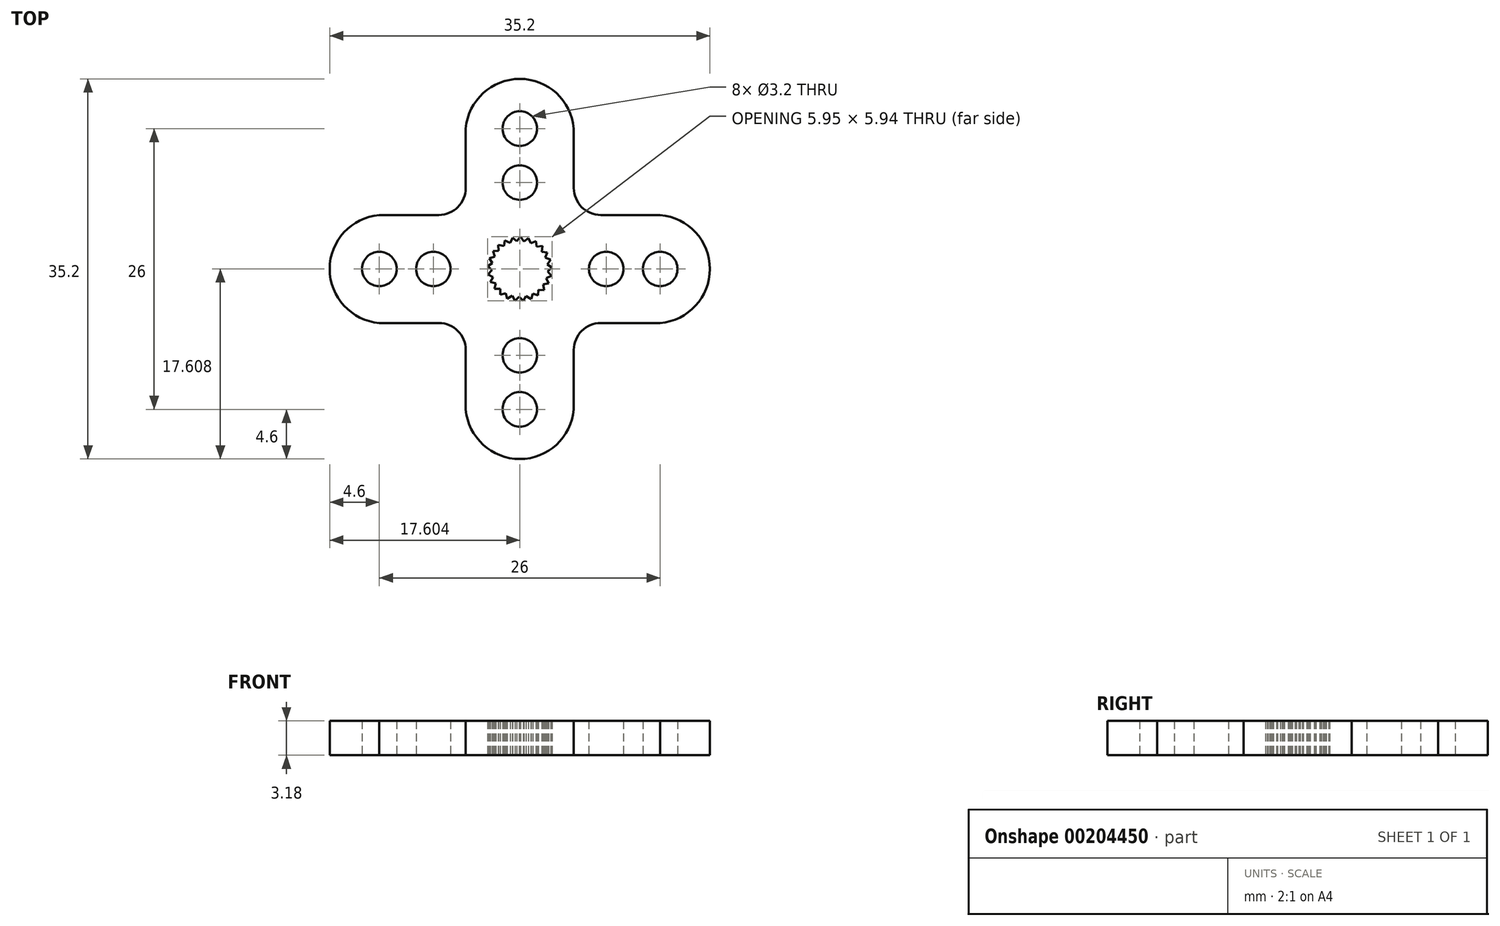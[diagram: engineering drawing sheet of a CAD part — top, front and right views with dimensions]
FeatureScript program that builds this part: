
annotation { "Feature Type Name" : "Feature", "Feature Type Description" : "" }
export const myFeature = defineFeature(function(context is Context, id is Id, definition is map)
    precondition{}
    {
        {
            var Q0;
            Q0=qCreatedBy(makeId("Top.planeOp"),FACE);
            var sketch = newSketch(context, id + "F0", { "sketchPlane" : qUnion([Q0])});
            skCircle(sketch, "E0", {"center": v(0, 13) * mm, "radius": 1.6 * mm});
            skCircle(sketch, "E1.0.1.0", {"center": v(0, 8) * mm, "radius": 1.6 * mm});
            skLineSegment(sketch, "E1.direction1", {"start": v(0, 13) * mm, "end": v(25, 13) * mm, "construction": true});
            skLineSegment(sketch, "E1.direction2", {"start": v(0, 13) * mm, "end": v(0, 8) * mm, "construction": true});
            skArc(sketch, "E2", {"start": v(5, 13) * mm, "mid": v(3.4, 16.28) * mm, "end": v(0, 17.6) * mm});
            skArc(sketch, "E3.MirrorCS", {"start": v(-5, 13) * mm, "mid": v(-3.4, 16.28) * mm, "end": v(0, 17.6) * mm});
            skPoint(sketch, "E4.center", {"position": v(0, 0) * mm});
            skLineSegment(sketch, "E5.trimOffspring", {"start": v(5, 7.5) * mm, "end": v(5, 13) * mm});
            skLineSegment(sketch, "E6.trimOffspring", {"start": v(-5, 7.5) * mm, "end": v(-5, 13) * mm});
            skArc(sketch, "E7", {"start": v(5, 7.5) * mm, "mid": v(5.73, 5.73) * mm, "end": v(7.5, 5) * mm});
            skArc(sketch, "E8.1.0", {"start": v(-7.5, 5) * mm, "mid": v(-5.73, 5.73) * mm, "end": v(-5, 7.5) * mm});
            skLineSegment(sketch, "E9", {"start": v(-2.48, 1.65) * mm, "end": v(-2.31, 1.15) * mm});
            skLineSegment(sketch, "E10", {"start": v(-2.31, 1.15) * mm, "end": v(-2.81, 0.98) * mm});
            skLineSegment(sketch, "E11.1.0", {"start": v(-2.81, 0.98) * mm, "end": v(-2.53, 0.54) * mm});
            skLineSegment(sketch, "E11.1.1", {"start": v(-2.53, 0.54) * mm, "end": v(-2.97, 0.25) * mm});
            skLineSegment(sketch, "E11.2.0", {"start": v(-2.97, 0.25) * mm, "end": v(-2.58, -0.1) * mm});
            skLineSegment(sketch, "E11.2.1", {"start": v(-2.58, -0.1) * mm, "end": v(-2.94, -0.5) * mm});
            skLineSegment(sketch, "E11.3.0", {"start": v(-2.94, -0.5) * mm, "end": v(-2.47, -0.74) * mm});
            skLineSegment(sketch, "E11.3.1", {"start": v(-2.47, -0.74) * mm, "end": v(-2.72, -1.2) * mm});
            skLineSegment(sketch, "E11.4.0", {"start": v(-2.72, -1.2) * mm, "end": v(-2.21, -1.34) * mm});
            skLineSegment(sketch, "E11.4.1", {"start": v(-2.21, -1.34) * mm, "end": v(-2.34, -1.85) * mm});
            skLineSegment(sketch, "E11.5.0", {"start": v(-2.34, -1.85) * mm, "end": v(-1.8, -1.84) * mm});
            skLineSegment(sketch, "E11.5.1", {"start": v(-1.8, -1.84) * mm, "end": v(-1.8, -2.37) * mm});
            skLineSegment(sketch, "E11.6.0", {"start": v(-1.8, -2.37) * mm, "end": v(-1.3, -2.24) * mm});
            skLineSegment(sketch, "E11.6.1", {"start": v(-1.3, -2.24) * mm, "end": v(-1.16, -2.75) * mm});
            skLineSegment(sketch, "E11.7.0", {"start": v(-1.16, -2.75) * mm, "end": v(-0.7, -2.49) * mm});
            skLineSegment(sketch, "E11.7.1", {"start": v(-0.7, -2.49) * mm, "end": v(-0.44, -2.95) * mm});
            skLineSegment(sketch, "E11.8.0", {"start": v(-0.44, -2.95) * mm, "end": v(-0.06, -2.58) * mm});
            skLineSegment(sketch, "E11.8.1", {"start": v(-0.06, -2.58) * mm, "end": v(0.3, -2.96) * mm});
            skLineSegment(sketch, "E11.9.0", {"start": v(0.3, -2.96) * mm, "end": v(0.59, -2.52) * mm});
            skLineSegment(sketch, "E11.9.1", {"start": v(0.59, -2.52) * mm, "end": v(1.04, -2.8) * mm});
            skLineSegment(sketch, "E11.10.0", {"start": v(1.04, -2.8) * mm, "end": v(1.2, -2.3) * mm});
            skLineSegment(sketch, "E11.10.1", {"start": v(1.2, -2.3) * mm, "end": v(1.7, -2.45) * mm});
            skLineSegment(sketch, "E11.11.0", {"start": v(1.7, -2.45) * mm, "end": v(1.73, -1.92) * mm});
            skLineSegment(sketch, "E11.11.1", {"start": v(1.73, -1.92) * mm, "end": v(2.25, -1.95) * mm});
            skLineSegment(sketch, "E11.12.0", {"start": v(2.25, -1.95) * mm, "end": v(2.15, -1.43) * mm});
            skLineSegment(sketch, "E11.12.1", {"start": v(2.15, -1.43) * mm, "end": v(2.67, -1.33) * mm});
            skLineSegment(sketch, "E11.13.0", {"start": v(2.67, -1.33) * mm, "end": v(2.44, -0.85) * mm});
            skLineSegment(sketch, "E11.13.1", {"start": v(2.44, -0.85) * mm, "end": v(2.91, -0.62) * mm});
            skLineSegment(sketch, "E11.14.0", {"start": v(2.91, -0.62) * mm, "end": v(2.57, -0.22) * mm});
            skLineSegment(sketch, "E11.14.1", {"start": v(2.57, -0.22) * mm, "end": v(2.98, 0.12) * mm});
            skLineSegment(sketch, "E11.15.0", {"start": v(2.98, 0.12) * mm, "end": v(2.55, 0.43) * mm});
            skLineSegment(sketch, "E11.15.1", {"start": v(2.55, 0.43) * mm, "end": v(2.85, 0.86) * mm});
            skLineSegment(sketch, "E11.16.0", {"start": v(2.85, 0.86) * mm, "end": v(2.36, 1.05) * mm});
            skLineSegment(sketch, "E11.16.1", {"start": v(2.36, 1.05) * mm, "end": v(2.55, 1.54) * mm});
            skLineSegment(sketch, "E11.17.0", {"start": v(2.55, 1.54) * mm, "end": v(2.03, 1.6) * mm});
            skLineSegment(sketch, "E11.17.1", {"start": v(2.03, 1.6) * mm, "end": v(2.09, 2.13) * mm});
            skLineSegment(sketch, "E11.18.0", {"start": v(2.09, 2.13) * mm, "end": v(1.56, 2.06) * mm});
            skLineSegment(sketch, "E11.18.1", {"start": v(1.56, 2.06) * mm, "end": v(1.5, 2.58) * mm});
            skLineSegment(sketch, "E11.19.0", {"start": v(1.5, 2.58) * mm, "end": v(1, 2.38) * mm});
            skLineSegment(sketch, "E11.19.1", {"start": v(1, 2.38) * mm, "end": v(0.8, 2.87) * mm});
            skLineSegment(sketch, "E11.20.0", {"start": v(0.8, 2.87) * mm, "end": v(0.38, 2.56) * mm});
            skLineSegment(sketch, "E11.20.1", {"start": v(0.38, 2.56) * mm, "end": v(0.07, 2.98) * mm});
            skLineSegment(sketch, "E11.21.0", {"start": v(0.07, 2.98) * mm, "end": v(-0.27, 2.57) * mm});
            skLineSegment(sketch, "E11.21.1", {"start": v(-0.27, 2.57) * mm, "end": v(-0.68, 2.9) * mm});
            skLineSegment(sketch, "E11.22.0", {"start": v(-0.68, 2.9) * mm, "end": v(-0.9, 2.42) * mm});
            skLineSegment(sketch, "E11.22.1", {"start": v(-0.9, 2.42) * mm, "end": v(-1.38, 2.64) * mm});
            skLineSegment(sketch, "E11.23.0", {"start": v(-1.38, 2.64) * mm, "end": v(-1.47, 2.12) * mm});
            skLineSegment(sketch, "E11.23.1", {"start": v(-1.47, 2.12) * mm, "end": v(-2, 2.22) * mm});
            skLineSegment(sketch, "E11.24.0", {"start": v(-2, 2.22) * mm, "end": v(-1.95, 1.69) * mm});
            skLineSegment(sketch, "E11.24.1", {"start": v(-1.95, 1.69) * mm, "end": v(-2.48, 1.65) * mm});
            skCircle(sketch, "E12.1.0", {"center": v(-13, 0) * mm, "radius": 1.6 * mm});
            skCircle(sketch, "E12.1.1", {"center": v(-8, 0) * mm, "radius": 1.6 * mm});
            skLineSegment(sketch, "E12.1.2", {"start": v(-13, 0) * mm, "end": v(-8, 0) * mm, "construction": true});
            skLineSegment(sketch, "E12.1.5", {"start": v(-7.5, 5) * mm, "end": v(-13, 5) * mm});
            skArc(sketch, "E12.1.6", {"start": v(-5, -7.5) * mm, "mid": v(-5.73, -5.73) * mm, "end": v(-7.5, -5) * mm});
            skLineSegment(sketch, "E12.1.9", {"start": v(-7.5, -5) * mm, "end": v(-13, -5) * mm});
            skArc(sketch, "E12.1.10", {"start": v(-13, -5) * mm, "mid": v(-16.28, -3.4) * mm, "end": v(-17.6, 0) * mm});
            skArc(sketch, "E12.1.11", {"start": v(-13, 5) * mm, "mid": v(-16.28, 3.4) * mm, "end": v(-17.6, 0) * mm});
            skCircle(sketch, "E12.2.0", {"center": v(0, -13) * mm, "radius": 1.6 * mm});
            skCircle(sketch, "E12.2.1", {"center": v(0, -8) * mm, "radius": 1.6 * mm});
            skLineSegment(sketch, "E12.2.2", {"start": v(0, -13) * mm, "end": v(0, -8) * mm, "construction": true});
            skArc(sketch, "E12.2.3", {"start": v(-5, -7.5) * mm, "mid": v(-5.73, -5.73) * mm, "end": v(-7.5, -5) * mm});
            skLineSegment(sketch, "E12.2.5", {"start": v(-5, -7.5) * mm, "end": v(-5, -13) * mm});
            skArc(sketch, "E12.2.6", {"start": v(7.5, -5) * mm, "mid": v(5.73, -5.73) * mm, "end": v(5, -7.5) * mm});
            skLineSegment(sketch, "E12.2.9", {"start": v(5, -7.5) * mm, "end": v(5, -13) * mm});
            skArc(sketch, "E12.2.10", {"start": v(5, -13) * mm, "mid": v(3.4, -16.28) * mm, "end": v(0, -17.6) * mm});
            skArc(sketch, "E12.2.11", {"start": v(-5, -13) * mm, "mid": v(-3.4, -16.28) * mm, "end": v(0, -17.6) * mm});
            skCircle(sketch, "E12.3.0", {"center": v(13, 0) * mm, "radius": 1.6 * mm});
            skCircle(sketch, "E12.3.1", {"center": v(8, 0) * mm, "radius": 1.6 * mm});
            skLineSegment(sketch, "E12.3.2", {"start": v(13, 0) * mm, "end": v(8, 0) * mm, "construction": true});
            skArc(sketch, "E12.3.3", {"start": v(7.5, -5) * mm, "mid": v(5.73, -5.73) * mm, "end": v(5, -7.5) * mm});
            skLineSegment(sketch, "E12.3.5", {"start": v(7.5, -5) * mm, "end": v(13, -5) * mm});
            skLineSegment(sketch, "E12.3.9", {"start": v(7.5, 5) * mm, "end": v(13, 5) * mm});
            skArc(sketch, "E12.3.10", {"start": v(13, 5) * mm, "mid": v(16.28, 3.4) * mm, "end": v(17.6, 0) * mm});
            skArc(sketch, "E12.3.11", {"start": v(13, -5) * mm, "mid": v(16.28, -3.4) * mm, "end": v(17.6, 0) * mm});
            skSolve(sketch);
        }
        {
            var Q0;
            Q0 = qSketchRegion(id + "F0", true);
            extrude(context, id + "F1", {"entities" : qUnion([Q0]), "depth" : 3.17 * mm});
        }
    });
